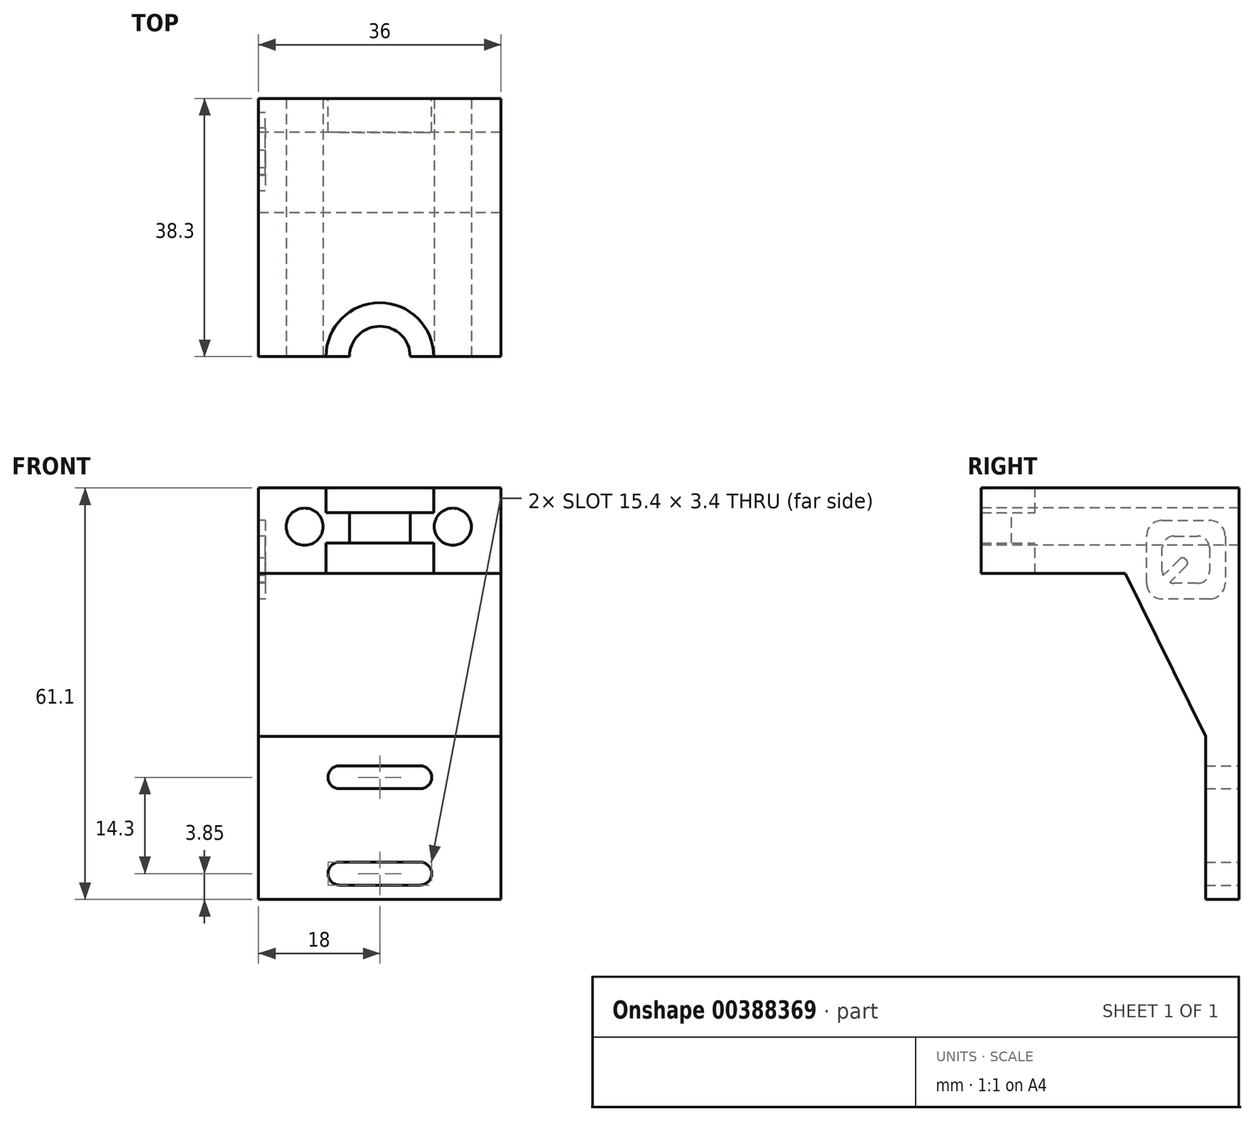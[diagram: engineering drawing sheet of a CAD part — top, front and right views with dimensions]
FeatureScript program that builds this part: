
annotation { "Feature Type Name" : "Feature", "Feature Type Description" : "" }
export const myFeature = defineFeature(function(context is Context, id is Id, definition is map)
    precondition{}
    {
        {
            var Q0;
            Q0=qCreatedBy(makeId("Front.planeOp"),FACE);
            var sketch = newSketch(context, id + "F0", { "sketchPlane" : qUnion([Q0])});
            skArc(sketch, "E0", {"start": v(-6, 16) * mm, "mid": v(-7.7, 14.3) * mm, "end": v(-6, 12.6) * mm});
            skArc(sketch, "E1", {"start": v(6, 12.6) * mm, "mid": v(7.7, 14.3) * mm, "end": v(6, 16) * mm});
            skArc(sketch, "E2", {"start": v(-6, 1.7) * mm, "mid": v(-7.7, 0) * mm, "end": v(-6, -1.7) * mm});
            skArc(sketch, "E3", {"start": v(6, -1.7) * mm, "mid": v(7.7, 0) * mm, "end": v(6, 1.7) * mm});
            skLineSegment(sketch, "E4", {"start": v(-6, 14.3) * mm, "end": v(6, 14.3) * mm, "construction": true});
            skLineSegment(sketch, "E5", {"start": v(6, 0) * mm, "end": v(6, 14.3) * mm, "construction": true});
            skLineSegment(sketch, "E6", {"start": v(-6, 0) * mm, "end": v(6, 0) * mm, "construction": true});
            skLineSegment(sketch, "E7", {"start": v(-6, 14.3) * mm, "end": v(-6, 0) * mm, "construction": true});
            skLineSegment(sketch, "E8.bottom", {"start": v(-15, 18.15) * mm, "end": v(15, 18.15) * mm});
            skLineSegment(sketch, "E8.top", {"start": v(-15, -3.85) * mm, "end": v(15, -3.85) * mm});
            skLineSegment(sketch, "E8.left", {"start": v(-15, 18.15) * mm, "end": v(-15, -3.85) * mm});
            skLineSegment(sketch, "E8.right", {"start": v(15, 18.15) * mm, "end": v(15, -3.85) * mm});
            skLineSegment(sketch, "E9", {"start": v(0, 14.3) * mm, "end": v(0, 18.15) * mm, "construction": true});
            skLineSegment(sketch, "E10", {"start": v(0, 0) * mm, "end": v(0, -3.85) * mm, "construction": true});
            skLineSegment(sketch, "E11", {"start": v(-6, 7.15) * mm, "end": v(-15, 7.15) * mm, "construction": true});
            skLineSegment(sketch, "E12", {"start": v(6, 7.15) * mm, "end": v(15, 7.15) * mm, "construction": true});
            skLineSegment(sketch, "E13", {"start": v(-6, 16) * mm, "end": v(6, 16) * mm});
            skLineSegment(sketch, "E14", {"start": v(-6, 12.6) * mm, "end": v(6, 12.6) * mm});
            skLineSegment(sketch, "E15", {"start": v(-6, 16) * mm, "end": v(-6, 12.6) * mm, "construction": true});
            skLineSegment(sketch, "E16", {"start": v(6, 16) * mm, "end": v(6, 12.6) * mm, "construction": true});
            skLineSegment(sketch, "E17", {"start": v(-6, 1.7) * mm, "end": v(6, 1.7) * mm});
            skLineSegment(sketch, "E18", {"start": v(-6, -1.7) * mm, "end": v(6, -1.7) * mm});
            skSolve(sketch);
        }
        {
            var Q0;
            Q0=makeQuery(id+"F0.imprint","IMPRINT",FACE,{"disambiguationData":[TD([[makeQuery(id+"F0.imprint","IMPRINT",EDGE,{"derivedFrom":sQuery(id+"F0.wireOp",EDGE,"E0")}),-1.0]])]});
            extrude(context, id + "F1", {"entities" : qUnion([Q0]), "depth" : 5 * mm});
        }
        {
            var Q0;
            Q0=makeQuery(id+"F1.opExtrude","SWEPT_FACE",FACE,{"disambiguationData":[OSD([sQuery(id+"F0.wireOp",EDGE,"E8.bottom")])]});
            extrude(context, id + "F2", {"entities" : qUnion([Q0]), "operationType" : NewBodyOperationType.ADD, "depth" : 39.1 * mm});
        }
        {
            var Q0;
            {var subQ0=sQuery(id+"F0.wireOp",EDGE,"E8.bottom");Q0=makeQuery(id+"F2.boolean.opBoolean","MERGE",FACE,{"derivedFrom":[makeQuery(id+"F1.opExtrude","CAP_FACE",FACE,{"disambiguationData":[OSD([sQuery(id+"F0.wireOp",EDGE,"E0"),sQuery(id+"F0.wireOp",EDGE,"E1"),sQuery(id+"F0.wireOp",EDGE,"E2"),sQuery(id+"F0.wireOp",EDGE,"E3"),subQ0,sQuery(id+"F0.wireOp",EDGE,"E8.top"),sQuery(id+"F0.wireOp",EDGE,"E8.left"),sQuery(id+"F0.wireOp",EDGE,"E8.right")])],"isStart":false}),makeQuery(id+"F2.opExtrude","SWEPT_FACE",FACE,{"disambiguationData":[OSD([subQ0]),TDD([makeQuery(id+"F1.opExtrude","CAP_EDGE",EDGE,{"disambiguationData":[OSD([subQ0])],"isStart":false})])]})]});}
            var sketch = newSketch(context, id + "F3", { "sketchPlane" : qUnion([Q0])});
            skLineSegment(sketch, "E19", {"start": v(-15, 44.55) * mm, "end": v(15, 44.55) * mm});
            skSolve(sketch);
        }
        {
            var Q0;
            {var subQ0=sQuery(id+"F3.wireOp",EDGE,"E19");Q0=makeQuery(id+"F3.imprint","IMPRINT",FACE,{"disambiguationData":[TD([[makeQuery(id+"F3.imprint","IMPRINT",EDGE,{"derivedFrom":subQ0}),1.0]])]});}
            extrude(context, id + "F4", {"entities" : qUnion([Q0]), "operationType" : NewBodyOperationType.ADD, "depth" : 50 * mm});
        }
        {
            var Q0;
            Q0=makeQuery(id+"F4.opExtrude","CAP_FACE",FACE,{"disambiguationData":[OSD([sQuery(id+"F0.wireOp",EDGE,"E8.bottom"),sQuery(id+"F0.wireOp",EDGE,"E8.left"),sQuery(id+"F0.wireOp",EDGE,"E8.right"),sQuery(id+"F3.wireOp",EDGE,"E19")])],"isStart":false});
            cPlane(context, id + "F5", {"entities" : qUnion([Q0]), "cplaneType" : CPlaneType.OFFSET, "offset" : 16.7 * mm, "oppositeDirection" : true, "width" : 150 * mm, "height" : 150 * mm});
        }
        {
            var Q0;
            Q0=qCreatedBy(id+"F5.planeOp",FACE);
            var sketch = newSketch(context, id + "F6", { "sketchPlane" : qUnion([Q0])});
            skLineSegment(sketch, "E20", {"start": v(0, 57.25) * mm, "end": v(8, 57.25) * mm});
            skLineSegment(sketch, "E21", {"start": v(8, 57.25) * mm, "end": v(8, 53.55) * mm});
            skLineSegment(sketch, "E22", {"start": v(8, 53.55) * mm, "end": v(4.5, 53.55) * mm});
            skLineSegment(sketch, "E23", {"start": v(4.5, 53.55) * mm, "end": v(4.5, 49.05) * mm});
            skLineSegment(sketch, "E24", {"start": v(4.5, 49.05) * mm, "end": v(8, 49.05) * mm});
            skLineSegment(sketch, "E25", {"start": v(8, 49.05) * mm, "end": v(8, 44.55) * mm});
            skLineSegment(sketch, "E26", {"start": v(8, 44.55) * mm, "end": v(0, 44.55) * mm});
            skLineSegment(sketch, "E27", {"start": v(0, 44.55) * mm, "end": v(0, 57.25) * mm});
            skSolve(sketch);
        }
        {
            var Q0;
            Q0=qSketchRegion(id+"F6",true);
            var Q1;
            Q1=sQuery(id+"F6.wireOp",EDGE,"E27");
            revolve(context, id + "F7", {"operationType" : NewBodyOperationType.REMOVE, "entities" : qUnion([Q0]), "axis" : qUnion([Q1]), "revolveType" : RevolveType.FULL, "oppositeDirection" : true});
        }
        {
            var Q0;
            {var subQ0=sQuery(id+"F0.wireOp",EDGE,"E8.bottom");Q0=makeQuery(id+"F2.boolean.opBoolean","MERGE",FACE,{"derivedFrom":[makeQuery(id+"F1.opExtrude","CAP_FACE",FACE,{"disambiguationData":[OSD([sQuery(id+"F0.wireOp",EDGE,"E0"),sQuery(id+"F0.wireOp",EDGE,"E1"),sQuery(id+"F0.wireOp",EDGE,"E2"),sQuery(id+"F0.wireOp",EDGE,"E3"),subQ0,sQuery(id+"F0.wireOp",EDGE,"E8.top"),sQuery(id+"F0.wireOp",EDGE,"E8.left"),sQuery(id+"F0.wireOp",EDGE,"E8.right")])],"isStart":true}),makeQuery(id+"F2.opExtrude","SWEPT_FACE",FACE,{"disambiguationData":[OSD([subQ0]),TDD([makeQuery(id+"F1.opExtrude","CAP_EDGE",EDGE,{"disambiguationData":[OSD([subQ0])],"isStart":true})])]})]});}
            var sketch = newSketch(context, id + "F8", { "sketchPlane" : qUnion([Q0])});
            skLineSegment(sketch, "E28", {"start": v(-15, 33.95) * mm, "end": v(15, 33.95) * mm});
            skLineSegment(sketch, "E29", {"start": v(-15, 38.95) * mm, "end": v(15, 38.95) * mm});
            skSolve(sketch);
        }
        {
            var Q0;
            {var subQ0=sQuery(id+"F8.wireOp",EDGE,"E28");Q0=makeQuery(id+"F8.imprint","IMPRINT",FACE,{"disambiguationData":[TD([[makeQuery(id+"F8.imprint","IMPRINT",EDGE,{"derivedFrom":subQ0}),1.0]])]});}
            extrude(context, id + "F9", {"entities" : qUnion([Q0]), "operationType" : NewBodyOperationType.ADD, "depth" : 25 * mm});
        }
        {
            var Q0;
            Q0=makeQuery(id+"F9.opExtrude","SWEPT_FACE",FACE,{"disambiguationData":[OSD([sQuery(id+"F8.wireOp",EDGE,"E28")])]});
            var sketch = newSketch(context, id + "F10", { "sketchPlane" : qUnion([Q0])});
            skLineSegment(sketch, "E30", {"start": v(-15, -20) * mm, "end": v(15, -20) * mm});
            skSolve(sketch);
        }
        {
            var Q0;
            {var subQ0=sQuery(id+"F10.wireOp",EDGE,"E30");Q0=makeQuery(id+"F10.imprint","IMPRINT",FACE,{"disambiguationData":[TD([[makeQuery(id+"F10.imprint","IMPRINT",EDGE,{"derivedFrom":subQ0}),-1.0]])]});}
            extrude(context, id + "F11", {"entities" : qUnion([Q0]), "operationType" : NewBodyOperationType.ADD, "depth" : 5 * mm});
        }
        {
            var Q0;
            {var subQ0=sQuery(id+"F8.wireOp",EDGE,"E28");Q0=makeQuery(id+"F11.boolean.opBoolean","MERGE",FACE,{"derivedFrom":[makeQuery(id+"F9.opExtrude","CAP_FACE",FACE,{"disambiguationData":[OSD([sQuery(id+"F0.wireOp",EDGE,"E8.bottom"),sQuery(id+"F0.wireOp",EDGE,"E8.left"),sQuery(id+"F0.wireOp",EDGE,"E8.right"),subQ0,sQuery(id+"F8.wireOp",EDGE,"E29")])],"isStart":false}),makeQuery(id+"F11.opExtrude","SWEPT_FACE",FACE,{"disambiguationData":[OSD([subQ0])]})]});}
            var sketch = newSketch(context, id + "F12", { "sketchPlane" : qUnion([Q0])});
            skLineSegment(sketch, "E31", {"start": v(-15, 33.95) * mm, "end": v(15, 33.95) * mm});
            skSolve(sketch);
        }
        {
            var Q0;
            {var subQ0=sQuery(id+"F12.wireOp",EDGE,"E31");Q0=makeQuery(id+"F12.imprint","IMPRINT",FACE,{"disambiguationData":[TD([[makeQuery(id+"F12.imprint","IMPRINT",EDGE,{"derivedFrom":subQ0}),-1.0]])]});}
            extrude(context, id + "F13", {"entities" : qUnion([Q0]), "operationType" : NewBodyOperationType.ADD, "depth" : 25 * mm});
        }
        {
            var Q0;
            Q0=makeQuery(id+"F13.opExtrude","SWEPT_FACE",FACE,{"disambiguationData":[OSD([sQuery(id+"F12.wireOp",EDGE,"E31")])]});
            var sketch = newSketch(context, id + "F14", { "sketchPlane" : qUnion([Q0])});
            skArc(sketch, "E32", {"start": v(-7.45, 38.32) * mm, "mid": v(-10.75, 37.5) * mm, "end": v(-7.45, 36.68) * mm});
            skArc(sketch, "E33", {"start": v(7.45, 36.68) * mm, "mid": v(10.75, 37.5) * mm, "end": v(7.45, 38.32) * mm});
            skLineSegment(sketch, "E34", {"start": v(-9, 37.5) * mm, "end": v(9, 37.5) * mm, "construction": true});
            skLineSegment(sketch, "E35", {"start": v(-9, 37.5) * mm, "end": v(-15, 37.5) * mm, "construction": true});
            skLineSegment(sketch, "E36", {"start": v(9, 37.5) * mm, "end": v(15, 37.5) * mm, "construction": true});
            skLineSegment(sketch, "E37", {"start": v(0, 50) * mm, "end": v(0, 25) * mm, "construction": true});
            skArc(sketch, "E38", {"start": v(-7.45, 36.68) * mm, "mid": v(0, 30) * mm, "end": v(7.45, 36.68) * mm});
            skArc(sketch, "E39.trimOffspring", {"start": v(7.45, 38.32) * mm, "mid": v(0, 45) * mm, "end": v(-7.45, 38.32) * mm});
            skSolve(sketch);
        }
        {
            var Q0;
            Q0=makeQuery(id+"F14.imprint","IMPRINT",FACE,{"disambiguationData":[TD([[makeQuery(id+"F14.imprint","IMPRINT",EDGE,{"derivedFrom":sQuery(id+"F14.wireOp",EDGE,"E32")}),1.0]])]});
            extrude(context, id + "F15", {"entities" : qUnion([Q0]), "operationType" : NewBodyOperationType.REMOVE, "oppositeDirection" : true, "depth" : 25 * mm});
        }
        {
            var Q0;
            {var subQ0=sQuery(id+"F8.wireOp",EDGE,"E28");var subQ1=sQuery(id+"F0.wireOp",EDGE,"E8.right");var subQ2=sQuery(id+"F0.wireOp",EDGE,"E8.bottom");Q0=makeQuery(id+"F13.boolean.opBoolean","MERGE",FACE,{"derivedFrom":[makeQuery(id+"F11.boolean.opBoolean","MERGE",FACE,{"derivedFrom":[makeQuery(id+"F9.boolean.opBoolean","MERGE",FACE,{"derivedFrom":[makeQuery(id+"F4.boolean.opBoolean","MERGE",FACE,{"derivedFrom":[makeQuery(id+"F2.boolean.opBoolean","MERGE",FACE,{"derivedFrom":[makeQuery(id+"F1.opExtrude","SWEPT_FACE",FACE,{"disambiguationData":[OSD([subQ1])]}),makeQuery(id+"F2.opExtrude","SWEPT_FACE",FACE,{"disambiguationData":[OSD([subQ2,subQ1])]})]}),makeQuery(id+"F4.opExtrude","SWEPT_FACE",FACE,{"disambiguationData":[OSD([subQ2,subQ1])]})]}),makeQuery(id+"F9.opExtrude","SWEPT_FACE",FACE,{"disambiguationData":[OSD([subQ2,subQ1])]})]}),makeQuery(id+"F11.opExtrude","SWEPT_FACE",FACE,{"disambiguationData":[OSD([subQ2,subQ1,subQ0])]})]}),makeQuery(id+"F13.opExtrude","SWEPT_FACE",FACE,{"disambiguationData":[OSD([subQ2,subQ1,subQ0])]})]});}
            extrude(context, id + "F16", {"entities" : qUnion([Q0]), "operationType" : NewBodyOperationType.ADD, "depth" : 3 * mm});
        }
        {
            var Q0;
            Q0=makeQuery(id+"F16.opExtrude","CAP_FACE",FACE,{"disambiguationData":[OSD([sQuery(id+"F0.wireOp",EDGE,"E8.bottom"),sQuery(id+"F0.wireOp",EDGE,"E8.right"),sQuery(id+"F8.wireOp",EDGE,"E28")])],"isStart":false});
            var sketch = newSketch(context, id + "F17", { "sketchPlane" : qUnion([Q0])});
            skLineSegment(sketch, "E40", {"start": v(0, 57.25) * mm, "end": v(50, 33.95) * mm});
            skSolve(sketch);
        }
        {
            var Q0;
            Q0=makeQuery(id+"F17.imprint","IMPRINT",FACE,{"disambiguationData":[TD([[makeQuery(id+"F17.imprint","IMPRINT",EDGE,{"derivedFrom":sQuery(id+"F17.wireOp",EDGE,"E40")}),-1.0]])]});
            extrude(context, id + "F18", {"entities" : qUnion([Q0]), "operationType" : NewBodyOperationType.ADD, "oppositeDirection" : true, "depth" : 3 * mm});
        }
        {
            var Q0;
            {var subQ0=sQuery(id+"F8.wireOp",EDGE,"E28");var subQ1=sQuery(id+"F0.wireOp",EDGE,"E8.left");var subQ2=sQuery(id+"F0.wireOp",EDGE,"E8.bottom");Q0=makeQuery(id+"F13.boolean.opBoolean","MERGE",FACE,{"derivedFrom":[makeQuery(id+"F11.boolean.opBoolean","MERGE",FACE,{"derivedFrom":[makeQuery(id+"F9.boolean.opBoolean","MERGE",FACE,{"derivedFrom":[makeQuery(id+"F4.boolean.opBoolean","MERGE",FACE,{"derivedFrom":[makeQuery(id+"F2.boolean.opBoolean","MERGE",FACE,{"derivedFrom":[makeQuery(id+"F1.opExtrude","SWEPT_FACE",FACE,{"disambiguationData":[OSD([subQ1])]}),makeQuery(id+"F2.opExtrude","SWEPT_FACE",FACE,{"disambiguationData":[OSD([subQ2,subQ1])]})]}),makeQuery(id+"F4.opExtrude","SWEPT_FACE",FACE,{"disambiguationData":[OSD([subQ2,subQ1])]})]}),makeQuery(id+"F9.opExtrude","SWEPT_FACE",FACE,{"disambiguationData":[OSD([subQ2,subQ1])]})]}),makeQuery(id+"F11.opExtrude","SWEPT_FACE",FACE,{"disambiguationData":[OSD([subQ2,subQ1,subQ0])]})]}),makeQuery(id+"F13.opExtrude","SWEPT_FACE",FACE,{"disambiguationData":[OSD([subQ2,subQ1,subQ0])]})]});}
            extrude(context, id + "F19", {"entities" : qUnion([Q0]), "operationType" : NewBodyOperationType.ADD, "depth" : 3 * mm});
        }
        {
            var Q0;
            Q0=makeQuery(id+"F19.opExtrude","CAP_FACE",FACE,{"disambiguationData":[OSD([sQuery(id+"F0.wireOp",EDGE,"E8.bottom"),sQuery(id+"F0.wireOp",EDGE,"E8.left"),sQuery(id+"F8.wireOp",EDGE,"E28")])],"isStart":false});
            var sketch = newSketch(context, id + "F20", { "sketchPlane" : qUnion([Q0])});
            skLineSegment(sketch, "E41", {"start": v(-50, 33.95) * mm, "end": v(0, 57.25) * mm});
            skSolve(sketch);
        }
        {
            var Q0;
            Q0=makeQuery(id+"F20.imprint","IMPRINT",FACE,{"disambiguationData":[TD([[makeQuery(id+"F20.imprint","IMPRINT",EDGE,{"derivedFrom":sQuery(id+"F20.wireOp",EDGE,"E41")}),-1.0]])]});
            extrude(context, id + "F21", {"entities" : qUnion([Q0]), "operationType" : NewBodyOperationType.ADD, "oppositeDirection" : true, "depth" : 3 * mm});
        }
        {
            var Q0;
            Q0=makeQuery(id+"F18.opExtrude","CAP_FACE",FACE,{"disambiguationData":[OSD([sQuery(id+"F0.wireOp",EDGE,"E8.bottom"),sQuery(id+"F0.wireOp",EDGE,"E8.right"),sQuery(id+"F8.wireOp",EDGE,"E28"),sQuery(id+"F8.wireOp",EDGE,"E29"),sQuery(id+"F12.wireOp",EDGE,"E31"),sQuery(id+"F17.wireOp",EDGE,"E40")])],"isStart":false});
            var sketch = newSketch(context, id + "F22", { "sketchPlane" : qUnion([Q0])});
            skLineSegment(sketch, "E42", {"start": v(-25, 38.95) * mm, "end": v(-25, 45.6) * mm});
            skSolve(sketch);
        }
        {
            var Q0;
            {var subQ0=sQuery(id+"F22.wireOp",EDGE,"E42");Q0=makeQuery(id+"F22.imprint","IMPRINT",FACE,{"disambiguationData":[TD([[makeQuery(id+"F22.imprint","IMPRINT",EDGE,{"derivedFrom":subQ0}),-1.0]])]});}
            extrude(context, id + "F23", {"entities" : qUnion([Q0]), "operationType" : NewBodyOperationType.ADD, "endBound" : BoundingType.UP_TO_NEXT, "depth" : 25 * mm});
        }
        {
            var Q0;
            Q0=makeQuery(id+"F4.opExtrude","CAP_FACE",FACE,{"disambiguationData":[OSD([sQuery(id+"F0.wireOp",EDGE,"E8.bottom"),sQuery(id+"F0.wireOp",EDGE,"E8.left"),sQuery(id+"F0.wireOp",EDGE,"E8.right"),sQuery(id+"F3.wireOp",EDGE,"E19")])],"isStart":false});
            var sketch = newSketch(context, id + "F24", { "sketchPlane" : qUnion([Q0])});
            skCircle(sketch, "E43", {"center": v(-11.16, 51.5) * mm, "radius": 2.75 * mm});
            skCircle(sketch, "E44", {"center": v(10.84, 51.5) * mm, "radius": 2.75 * mm});
            skLineSegment(sketch, "E45", {"start": v(-11.16, 51.5) * mm, "end": v(10.84, 51.5) * mm, "construction": true});
            skLineSegment(sketch, "E46", {"start": v(0, 57.25) * mm, "end": v(-0.16, 44.55) * mm, "construction": true});
            skPoint(sketch, "E46.endSnap0", {"position": v(-0.16, 51.5) * mm});
            skSolve(sketch);
        }
        {
            var Q0;
            Q0=makeQuery(id+"F24.imprint","IMPRINT",FACE,{"disambiguationData":[TD([[makeQuery(id+"F24.imprint","IMPRINT",EDGE,{"derivedFrom":sQuery(id+"F24.wireOp",EDGE,"E43")}),1.0]])]});
            var Q1;
            Q1=makeQuery(id+"F24.imprint","IMPRINT",FACE,{"disambiguationData":[TD([[makeQuery(id+"F24.imprint","IMPRINT",EDGE,{"derivedFrom":sQuery(id+"F24.wireOp",EDGE,"E44")}),1.0]])]});
            extrude(context, id + "F25", {"entities" : qUnion([Q0, Q1]), "operationType" : NewBodyOperationType.REMOVE, "oppositeDirection" : true, "depth" : 500 * mm});
        }
        {
            var Q0;
            Q0=qCreatedBy(id+"F5.planeOp",FACE);
            var sketch = newSketch(context, id + "F26", { "sketchPlane" : qUnion([Q0])});
            skLineSegment(sketch, "E47.bottom", {"start": v(-33.75, 65.72) * mm, "end": v(34.34, 65.72) * mm});
            skLineSegment(sketch, "E47.top", {"start": v(-33.75, -7.1) * mm, "end": v(34.34, -7.1) * mm});
            skLineSegment(sketch, "E47.left", {"start": v(-33.75, 65.72) * mm, "end": v(-33.75, -7.1) * mm});
            skLineSegment(sketch, "E47.right", {"start": v(34.34, 65.72) * mm, "end": v(34.34, -7.1) * mm});
            skSolve(sketch);
        }
        {
            var Q0;
            Q0=makeQuery(id+"F26.imprint","IMPRINT",FACE,{"disambiguationData":[TD([[makeQuery(id+"F26.imprint","IMPRINT",EDGE,{"derivedFrom":sQuery(id+"F26.wireOp",EDGE,"E47.bottom")}),-1.0]])]});
            extrude(context, id + "F27", {"entities" : qUnion([Q0]), "operationType" : NewBodyOperationType.REMOVE, "depth" : 25 * mm});
        }
        {
            var Q0;
            {var subQ0=sQuery(id+"F8.wireOp",EDGE,"E28");var subQ1=sQuery(id+"F0.wireOp",EDGE,"E8.left");var subQ2=sQuery(id+"F0.wireOp",EDGE,"E8.bottom");Q0=makeQuery(id+"F21.boolean.opBoolean","MERGE",FACE,{"derivedFrom":[makeQuery(id+"F19.opExtrude","CAP_FACE",FACE,{"disambiguationData":[OSD([subQ2,subQ1,subQ0])],"isStart":false}),makeQuery(id+"F21.opExtrude","CAP_FACE",FACE,{"disambiguationData":[OSD([subQ2,subQ1,subQ0,sQuery(id+"F8.wireOp",EDGE,"E29"),sQuery(id+"F12.wireOp",EDGE,"E31"),sQuery(id+"F20.wireOp",EDGE,"E41")])],"isStart":true})]});}
            var sketch = newSketch(context, id + "F28", { "sketchPlane" : qUnion([Q0])});
            skLineSegment(sketch, "E48", {"start": v(5, 20.35) * mm, "end": v(16.93, 44.55) * mm});
            skSolve(sketch);
        }
        {
            var Q0;
            {var subQ0=sQuery(id+"F28.wireOp",EDGE,"E48");Q0=makeQuery(id+"F28.imprint","IMPRINT",FACE,{"disambiguationData":[TD([[makeQuery(id+"F28.imprint","IMPRINT",EDGE,{"derivedFrom":subQ0}),1.0]])]});}
            extrude(context, id + "F29", {"entities" : qUnion([Q0]), "operationType" : NewBodyOperationType.ADD, "oppositeDirection" : true, "depth" : 36 * mm});
        }
        {
            var Q0;
            Q0=makeQuery(id+"F29.opExtrude","SWEPT_EDGE",EDGE,{"disambiguationData":[OSD([sQuery(id+"F0.wireOp",EDGE,"E8.bottom"),sQuery(id+"F0.wireOp",EDGE,"E8.left"),sQuery(id+"F3.wireOp",EDGE,"E19"),sQuery(id+"F28.wireOp",EDGE,"E48")])]});
            var Q1;
            Q1=makeQuery(id+"F29.opExtrude","SWEPT_EDGE",EDGE,{"disambiguationData":[OSD([sQuery(id+"F0.wireOp",EDGE,"E8.bottom"),sQuery(id+"F0.wireOp",EDGE,"E8.left"),sQuery(id+"F28.wireOp",EDGE,"E48")])]});
            var Q2;
            {var subQ0=sQuery(id+"F10.wireOp",EDGE,"E30");var subQ1=sQuery(id+"F8.wireOp",EDGE,"E28");var subQ2=sQuery(id+"F0.wireOp",EDGE,"E8.left");var subQ3=sQuery(id+"F0.wireOp",EDGE,"E8.bottom");var subQ4=sQuery(id+"F0.wireOp",EDGE,"E8.right");Q2=makeQuery(id+"F19.boolean.opBoolean","MERGE",EDGE,{"derivedFrom":[makeQuery(id+"F16.boolean.opBoolean","MERGE",EDGE,{"derivedFrom":[makeQuery(id+"F11.opExtrude","CAP_EDGE",EDGE,{"disambiguationData":[OSD([subQ0])],"isStart":true}),makeQuery(id+"F16.opExtrude","SWEPT_EDGE",EDGE,{"disambiguationData":[OSD([subQ3,subQ4,subQ1,subQ0]),TDD([makeQuery(id+"F11.opExtrude","CAP_VERTEX",VERTEX,{"disambiguationData":[OSD([subQ3,subQ4,subQ1,subQ0])],"isStart":true})])]})]}),makeQuery(id+"F19.opExtrude","SWEPT_EDGE",EDGE,{"disambiguationData":[OSD([subQ3,subQ2,subQ1,subQ0]),TDD([makeQuery(id+"F11.opExtrude","CAP_VERTEX",VERTEX,{"disambiguationData":[OSD([subQ3,subQ2,subQ1,subQ0])],"isStart":true})])]})]});}
            var Q3;
            {var subQ0=sQuery(id+"F8.wireOp",EDGE,"E28");var subQ1=sQuery(id+"F0.wireOp",EDGE,"E8.left");var subQ2=sQuery(id+"F0.wireOp",EDGE,"E8.bottom");var subQ3=sQuery(id+"F0.wireOp",EDGE,"E8.right");Q3=makeQuery(id+"F19.boolean.opBoolean","MERGE",EDGE,{"derivedFrom":[makeQuery(id+"F16.boolean.opBoolean","MERGE",EDGE,{"derivedFrom":[makeQuery(id+"F9.opExtrude","CAP_EDGE",EDGE,{"disambiguationData":[OSD([subQ0])],"isStart":true}),makeQuery(id+"F16.opExtrude","SWEPT_EDGE",EDGE,{"disambiguationData":[OSD([subQ2,subQ3,subQ0]),TDD([makeQuery(id+"F9.opExtrude","CAP_VERTEX",VERTEX,{"disambiguationData":[OSD([subQ2,subQ3,subQ0])],"isStart":true})])]})]}),makeQuery(id+"F19.opExtrude","SWEPT_EDGE",EDGE,{"disambiguationData":[OSD([subQ2,subQ1,subQ0]),TDD([makeQuery(id+"F9.opExtrude","CAP_VERTEX",VERTEX,{"disambiguationData":[OSD([subQ2,subQ1,subQ0])],"isStart":true})])]})]});}
            fillet(context, id + "F30", {"entities" : qUnion([Q0, Q1, Q2, Q3]), "radius" : 5 * mm, "tangentPropagation" : true, "allowEdgeOverflow" : false});
        }
        {
            var Q0;
            {var subQ0=sQuery(id+"F0.wireOp",EDGE,"E8.left");var subQ1=sQuery(id+"F0.wireOp",EDGE,"E8.bottom");var subQ2=sQuery(id+"F8.wireOp",EDGE,"E28");Q0=makeQuery(id+"F29.boolean.opBoolean","MERGE",FACE,{"derivedFrom":[makeQuery(id+"F21.boolean.opBoolean","MERGE",FACE,{"derivedFrom":[makeQuery(id+"F19.opExtrude","CAP_FACE",FACE,{"disambiguationData":[OSD([subQ1,subQ0,subQ2])],"isStart":false}),makeQuery(id+"F21.opExtrude","CAP_FACE",FACE,{"disambiguationData":[OSD([subQ1,subQ0,subQ2,sQuery(id+"F8.wireOp",EDGE,"E29"),sQuery(id+"F12.wireOp",EDGE,"E31"),sQuery(id+"F20.wireOp",EDGE,"E41")])],"isStart":true})]}),makeQuery(id+"F29.opExtrude","CAP_FACE",FACE,{"disambiguationData":[OSD([subQ1,subQ0,sQuery(id+"F3.wireOp",EDGE,"E19"),sQuery(id+"F28.wireOp",EDGE,"E48")])],"isStart":true})]});}
            var sketch = newSketch(context, id + "F31", { "sketchPlane" : qUnion([Q0])});
            skLineSegment(sketch, "E49", {"start": v(4.42, 40.77) * mm, "end": v(11.42, 40.77) * mm});
            skLineSegment(sketch, "E50", {"start": v(13.75, 43.1) * mm, "end": v(13.75, 50.1) * mm});
            skLineSegment(sketch, "E51", {"start": v(11.42, 52.44) * mm, "end": v(4.42, 52.44) * mm});
            skLineSegment(sketch, "E52", {"start": v(2.08, 50.1) * mm, "end": v(2.08, 43.1) * mm});
            skArc(sketch, "E53", {"start": v(4.42, 52.44) * mm, "mid": v(2.77, 51.75) * mm, "end": v(2.08, 50.1) * mm});
            skArc(sketch, "E54", {"start": v(13.75, 50.1) * mm, "mid": v(13.07, 51.75) * mm, "end": v(11.42, 52.44) * mm});
            skArc(sketch, "E55", {"start": v(2.08, 43.1) * mm, "mid": v(2.77, 41.45) * mm, "end": v(4.42, 40.77) * mm});
            skArc(sketch, "E56", {"start": v(11.42, 40.77) * mm, "mid": v(13.07, 41.45) * mm, "end": v(13.75, 43.1) * mm});
            skLineSegment(sketch, "E57", {"start": v(6.17, 43.1) * mm, "end": v(9.67, 43.1) * mm});
            skLineSegment(sketch, "E58", {"start": v(11.42, 44.85) * mm, "end": v(11.42, 48.35) * mm});
            skLineSegment(sketch, "E59", {"start": v(9.67, 50.1) * mm, "end": v(6.17, 50.1) * mm});
            skLineSegment(sketch, "E60", {"start": v(4.42, 48.35) * mm, "end": v(4.42, 44.85) * mm});
            skArc(sketch, "E61", {"start": v(6.17, 50.1) * mm, "mid": v(4.93, 49.6) * mm, "end": v(4.42, 48.35) * mm});
            skArc(sketch, "E62", {"start": v(11.42, 48.35) * mm, "mid": v(10.9, 49.6) * mm, "end": v(9.67, 50.1) * mm});
            skArc(sketch, "E63", {"start": v(4.42, 44.85) * mm, "mid": v(4.93, 43.62) * mm, "end": v(6.17, 43.1) * mm});
            skLineSegment(sketch, "E64", {"start": v(7.92, 46.6) * mm, "end": v(8, 46.69) * mm});
            skLineSegment(sketch, "E65", {"start": v(8.82, 46.69) * mm, "end": v(11.3, 44.21) * mm});
            skLineSegment(sketch, "E66", {"start": v(7.83, 45.7) * mm, "end": v(10.3, 43.22) * mm});
            skArc(sketch, "E67", {"start": v(8.82, 46.69) * mm, "mid": v(8.41, 46.86) * mm, "end": v(8, 46.69) * mm});
            skArc(sketch, "E68", {"start": v(7.83, 46.52) * mm, "mid": v(7.66, 46.1) * mm, "end": v(7.83, 45.7) * mm});
            skArc(sketch, "E69", {"start": v(9.67, 43.1) * mm, "mid": v(10, 43.13) * mm, "end": v(10.3, 43.22) * mm});
            skArc(sketch, "E70", {"start": v(11.3, 44.21) * mm, "mid": v(11.39, 44.53) * mm, "end": v(11.42, 44.85) * mm});
            skLineSegment(sketch, "E71", {"start": v(7.83, 46.52) * mm, "end": v(7.92, 46.6) * mm});
            skSolve(sketch);
        }
        {
            var Q0;
            Q0=qSketchRegion(id+"F31",true);
            extrude(context, id + "F32", {"entities" : qUnion([Q0]), "operationType" : NewBodyOperationType.REMOVE, "oppositeDirection" : true, "depth" : 1 * mm});
        }
        {
            var Q0;
            {var subQ0=sQuery(id+"F8.wireOp",EDGE,"E28");var subQ1=sQuery(id+"F0.wireOp",EDGE,"E8.left");var subQ2=sQuery(id+"F0.wireOp",EDGE,"E8.bottom");var subQ3=sQuery(id+"F0.wireOp",EDGE,"E8.right");Q0=makeQuery(id+"F19.boolean.opBoolean","MERGE",FACE,{"derivedFrom":[makeQuery(id+"F16.boolean.opBoolean","MERGE",FACE,{"derivedFrom":[makeQuery(id+"F13.opExtrude","CAP_FACE",FACE,{"disambiguationData":[OSD([subQ2,subQ1,subQ3,subQ0,sQuery(id+"F12.wireOp",EDGE,"E31")])],"isStart":false}),makeQuery(id+"F16.opExtrude","SWEPT_FACE",FACE,{"disambiguationData":[OSD([subQ2,subQ3,subQ0]),TDD([makeQuery(id+"F13.opExtrude","CAP_EDGE",EDGE,{"disambiguationData":[OSD([subQ2,subQ3,subQ0])],"isStart":false})])]})]}),makeQuery(id+"F19.opExtrude","SWEPT_FACE",FACE,{"disambiguationData":[OSD([subQ2,subQ1,subQ0]),TDD([makeQuery(id+"F13.opExtrude","CAP_EDGE",EDGE,{"disambiguationData":[OSD([subQ2,subQ1,subQ0])],"isStart":false})])]})]});}
            var sketch = newSketch(context, id + "F33", { "sketchPlane" : qUnion([Q0])});
            skLineSegment(sketch, "E72.bottom", {"start": v(-36.41, 60.99) * mm, "end": v(45.89, 60.99) * mm});
            skLineSegment(sketch, "E72.top", {"start": v(-36.41, -14.5) * mm, "end": v(45.89, -14.5) * mm});
            skLineSegment(sketch, "E72.left", {"start": v(-36.41, 60.99) * mm, "end": v(-36.41, -14.5) * mm});
            skLineSegment(sketch, "E72.right", {"start": v(45.89, 60.99) * mm, "end": v(45.89, -14.5) * mm});
            skSolve(sketch);
        }
        {
            var Q0;
            Q0=makeQuery(id+"F33.imprint","IMPRINT",FACE,{"disambiguationData":[TD([[makeQuery(id+"F33.imprint","IMPRINT",EDGE,{"derivedFrom":sQuery(id+"F33.wireOp",EDGE,"E72.bottom")}),-1.0]])]});
            var Q1;
            {var subQ0=sQuery(id+"F8.wireOp",EDGE,"E28");var subQ2=sQuery(id+"F0.wireOp",EDGE,"E8.bottom");var subQ3=sQuery(id+"F0.wireOp",EDGE,"E8.right");Q1=makeQuery(id+"F33.imprint","IMPRINT",FACE,{"disambiguationData":[TD([[makeQuery(id+"F33.imprint","IMPRINT",EDGE,{"derivedFrom":makeQuery(id+"F16.opExtrude","CAP_EDGE",EDGE,{"disambiguationData":[OSD([subQ2,subQ3,subQ0]),TDD([makeQuery(id+"F13.opExtrude","CAP_EDGE",EDGE,{"disambiguationData":[OSD([subQ2,subQ3,subQ0])],"isStart":false})])],"isStart":false})}),1.0]])]});}
            extrude(context, id + "F34", {"entities" : qUnion([Q0, Q1]), "operationType" : NewBodyOperationType.REMOVE, "oppositeDirection" : true, "depth" : 50 * mm});
        }
    });
